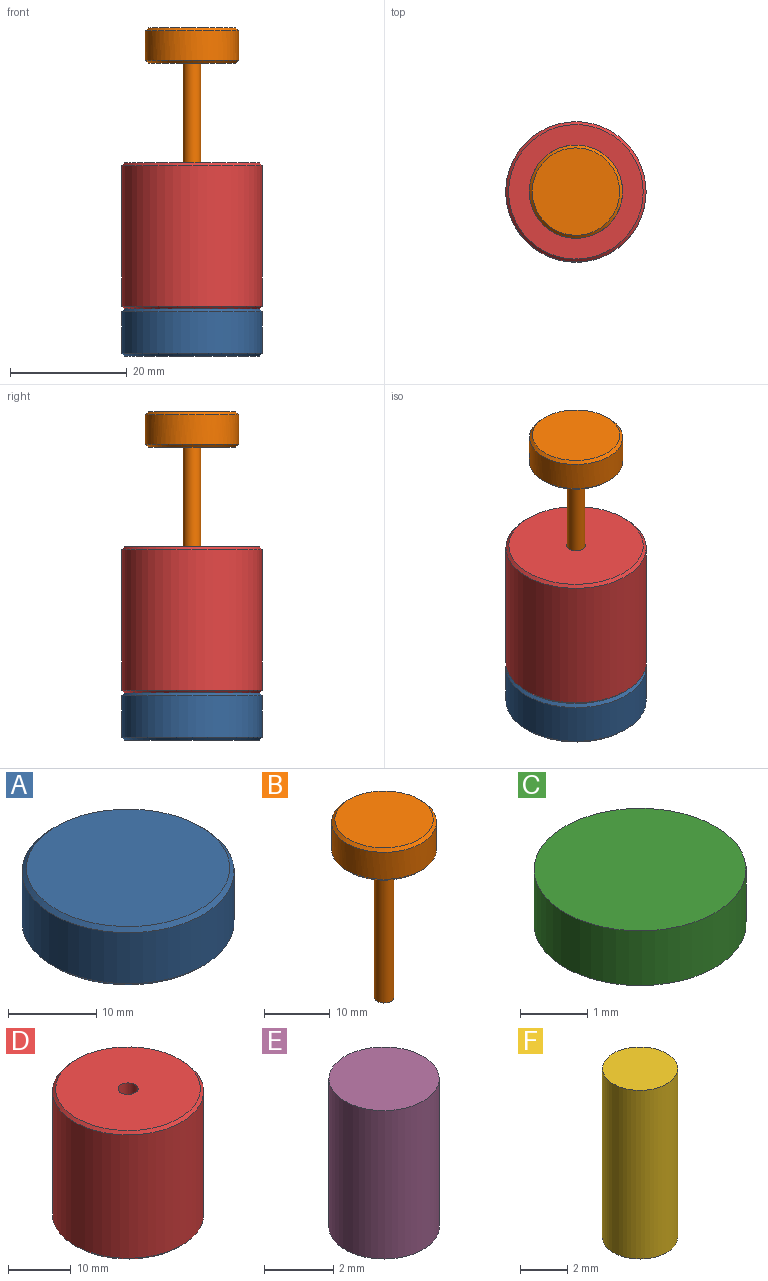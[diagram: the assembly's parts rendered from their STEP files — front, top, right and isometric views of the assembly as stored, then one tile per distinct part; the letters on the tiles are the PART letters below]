
ASSEMBLY  parts=6 mates=10
PART A: 5 faces, bbox 24x24x8.1 mm
  f0: cylinder r=12mm len=24mm, axis (0,0,1), area 533.1mm2, adj f3,f4
  f1: plane 23x23mm, normal (0,0,-1), area 415.5mm2, adj f3
  f2: plane 23x23mm, normal (0,0,1), area 415.5mm2, adj f4
  f3: cone r=12mm half-angle=45deg, axis (0,0,1), area 52.2mm2, adj f0,f1
  f4: cone r=11.5mm half-angle=45deg, axis (0,0,-1), area 52.2mm2, adj f0,f2
PART B: 7 faces, bbox 16x16x33.1 mm
  f0: cylinder r=7.98mm len=15.96mm, axis (0,0,1), area 251.7mm2, adj f5,f6
  f1: plane 14.96x14.96mm, normal (0,0,1), area 175.8mm2, adj f5
  f2: cylinder r=1.5mm len=27.12mm, axis (0,0,-1), area 254.7mm2, adj f3,f4
  f3: plane 14.96x14.96mm, normal (0,0,-1), area 168.8mm2, adj f2,f6
  f4: plane 2.99x2.99mm, normal (0,0,-1), area 7mm2, adj f2
  f5: cone r=7.48mm half-angle=45deg, axis (0,0,-1), area 34.3mm2, adj f0,f1
  f6: cone r=7.98mm half-angle=45deg, axis (0,0,1), area 34.3mm2, adj f0,f3
PART C: 3 faces, bbox 3.2x3.2x1 mm
  f0: cylinder r=1.58mm len=3.17mm, axis (0,0,-1), area 9.9mm2, adj f1,f2
  f1: plane 3.17x3.17mm, normal (0,0,1), area 7.9mm2, adj f0
  f2: plane 3.17x3.17mm, normal (0,0,-1), area 7.9mm2, adj f0
PART D: 6 faces, bbox 24x24x25 mm
  f0: cylinder r=12.01mm len=24.01mm, axis (0,0,-1), area 1810.3mm2, adj f3,f4
  f1: plane 23.01x23.01mm, normal (0,0,1), area 407.9mm2, adj f4,f5
  f2: plane 23.01x23.01mm, normal (0,0,-1), area 407.9mm2, adj f3,f5
  f3: cone r=12.01mm half-angle=45deg, axis (0,0,1), area 52.2mm2, adj f0,f2
  f4: cone r=11.5mm half-angle=45deg, axis (0,0,-1), area 52.2mm2, adj f0,f1
  f5: cylinder r=1.59mm len=25mm, axis (0,0,1), area 250mm2, adj f1,f2
PART E: 3 faces, bbox 3.2x3.2x5.2 mm
  f0: cylinder r=1.59mm len=5.24mm, axis (0,0,1), area 52.3mm2, adj f1,f2
  f1: plane 3.18x3.18mm, normal (0,0,-1), area 7.9mm2, adj f0
  f2: plane 3.18x3.18mm, normal (0,0,1), area 7.9mm2, adj f0
PART F: 3 faces, bbox 3.2x3.2x8.7 mm
  f0: cylinder r=1.59mm len=8.73mm, axis (0,0,1), area 87.2mm2, adj f1,f2
  f1: plane 3.18x3.18mm, normal (0,0,-1), area 7.9mm2, adj f0
  f2: plane 3.18x3.18mm, normal (0,0,1), area 7.9mm2, adj f0
PLACE A t=(-11.07,19.45,-21.2)mm
PLACE B t=(-11.07,19.45,26.91)mm
PLACE C t=(-11.07,19.45,-15.96)mm
PLACE D t=(-11.07,19.45,-21.2)mm fixed
PLACE E t=(-11.07,19.45,-15.96)mm
PLACE F t=(-11.07,19.45,-6.23)mm
MATE planar E.f0 <-> A.f0  axis (0,0,-1) through (-11.07,19.45,-21.2)mm
MATE cylindrical A.f0 <-> D.f0  axis (0,0,1) through (-11.07,19.45,-25.24)mm
MATE cylindrical C.f0 <-> D.f5  axis (0,0,-1) through (-11.07,19.45,-15.46)mm
MATE planar F.f0 <-> C.f0  axis (0,0,-1) through (-11.07,19.45,-14.96)mm
MATE planar D.f0 <-> A.f0  axis (0,0,-1) through (-11.07,19.45,-21.2)mm
MATE cylindrical B.f2 <-> D.f5  axis (0,0,-1) through (-11.07,19.45,-6.23)mm
MATE planar B.f2 <-> F.f0  axis (0,0,-1) through (-11.07,19.45,-6.23)mm
MATE cylindrical E.f0 <-> D.f5  axis (0,0,1) through (-11.07,19.45,-18.58)mm
MATE planar C.f0 <-> E.f0  axis (0,0,-1) through (-11.07,19.45,-15.96)mm
MATE cylindrical F.f0 <-> D.f5  axis (0,0,1) through (-11.07,19.45,-10.6)mm
